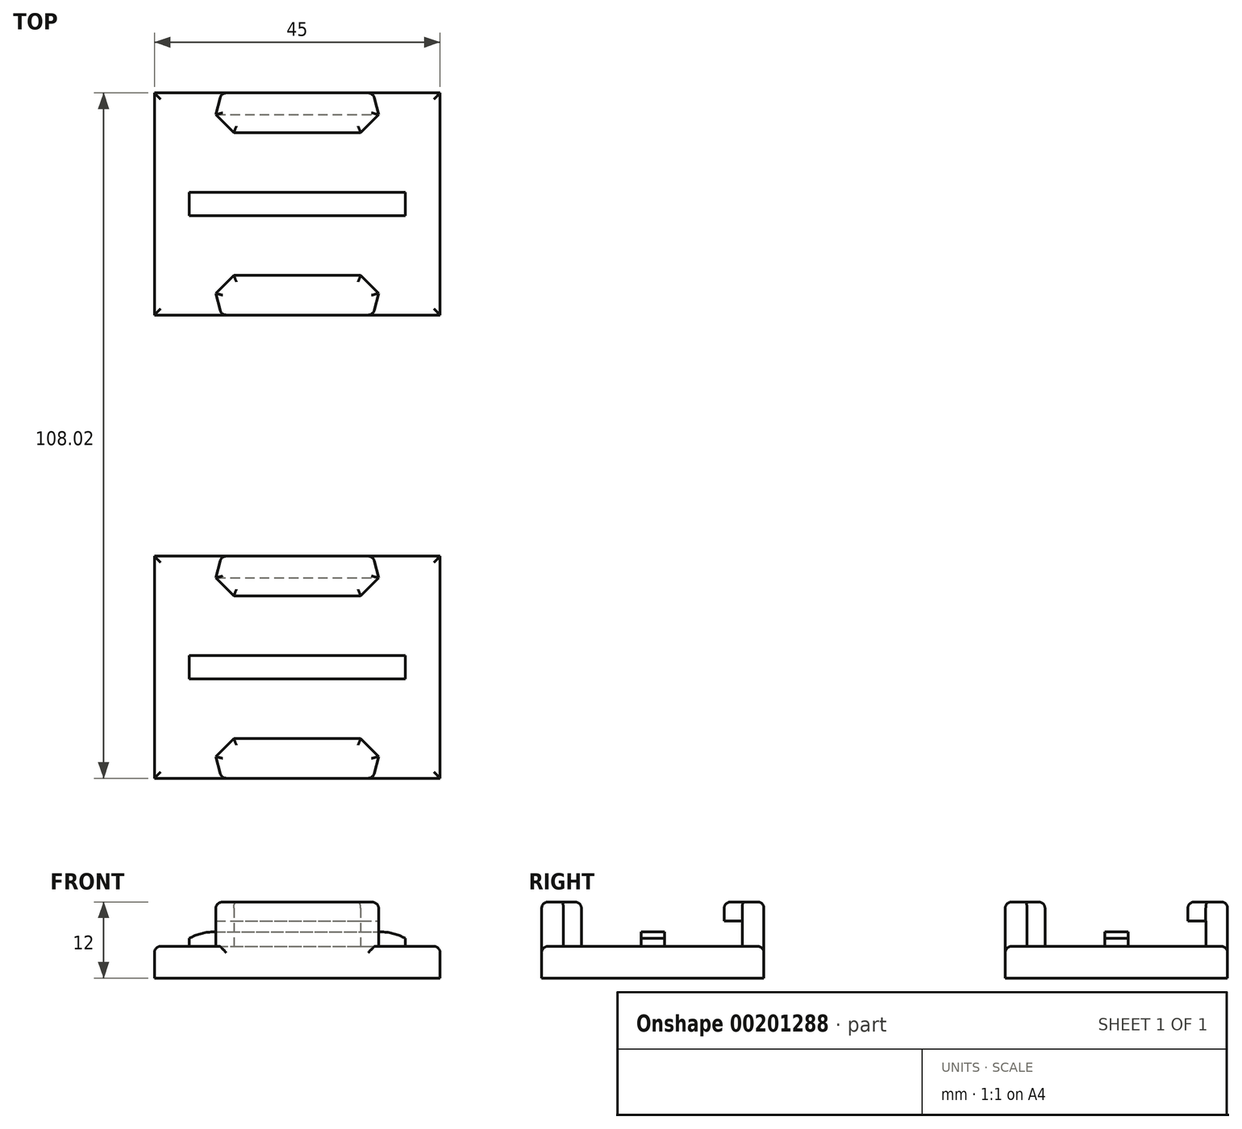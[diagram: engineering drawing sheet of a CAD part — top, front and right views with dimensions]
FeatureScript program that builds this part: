
annotation { "Feature Type Name" : "Feature", "Feature Type Description" : "" }
export const myFeature = defineFeature(function(context is Context, id is Id, definition is map)
    precondition{}
    {
        {
            var Q0;
            Q0=qCreatedBy(makeId("Top.planeOp"),FACE);
            var sketch = newSketch(context, id + "F0", { "sketchPlane" : qUnion([Q0])});
            skLineSegment(sketch, "E0.rect.bottom", {"start": v(-22.5, 17.5) * mm, "end": v(22.5, 17.5) * mm});
            skLineSegment(sketch, "E0.rect.top", {"start": v(-22.5, -17.5) * mm, "end": v(22.5, -17.5) * mm});
            skLineSegment(sketch, "E0.rect.left", {"start": v(-22.5, 17.5) * mm, "end": v(-22.5, -17.5) * mm});
            skLineSegment(sketch, "E0.rect.right", {"start": v(22.5, 17.5) * mm, "end": v(22.5, -17.5) * mm});
            skPoint(sketch, "E0.rect.middle", {"position": v(0, 0) * mm});
            skSolve(sketch);
        }
        {
            var Q0;
            Q0=makeQuery(id+"F0.imprint","IMPRINT",FACE,{"disambiguationData":[TD([[makeQuery(id+"F0.imprint","IMPRINT",EDGE,{"derivedFrom":sQuery(id+"F0.wireOp",EDGE,"E0.rect.bottom")}),-1.0]])]});
            extrude(context, id + "F1", {"entities" : qUnion([Q0]), "depth" : 5 * mm});
        }
        {
            var Q0;
            Q0=makeQuery(id+"F1.opExtrude","CAP_FACE",FACE,{"disambiguationData":[OSD([sQuery(id+"F0.wireOp",EDGE,"E0.rect.bottom"),sQuery(id+"F0.wireOp",EDGE,"E0.rect.top"),sQuery(id+"F0.wireOp",EDGE,"E0.rect.left"),sQuery(id+"F0.wireOp",EDGE,"E0.rect.right")])],"isStart":false});
            var sketch = newSketch(context, id + "F2", { "sketchPlane" : qUnion([Q0])});
            skLineSegment(sketch, "E1.rect.bottom", {"start": v(-17, 1.82) * mm, "end": v(17, 1.82) * mm});
            skLineSegment(sketch, "E1.rect.top", {"start": v(-17, -1.83) * mm, "end": v(17, -1.83) * mm});
            skLineSegment(sketch, "E1.rect.left", {"start": v(-17, 1.82) * mm, "end": v(-17, -1.83) * mm});
            skLineSegment(sketch, "E1.rect.right", {"start": v(17, 1.82) * mm, "end": v(17, -1.83) * mm});
            skPoint(sketch, "E1.rect.middle", {"position": v(0, 0) * mm});
            skSolve(sketch);
        }
        {
            var Q0;
            Q0=makeQuery(id+"F2.imprint","IMPRINT",FACE,{"disambiguationData":[TD([[makeQuery(id+"F2.imprint","IMPRINT",EDGE,{"derivedFrom":sQuery(id+"F2.wireOp",EDGE,"E1.rect.bottom")}),-1.0]])]});
            extrude(context, id + "F3", {"entities" : qUnion([Q0]), "operationType" : NewBodyOperationType.ADD, "depth" : 2.25 * mm});
        }
        {
            var Q0;
            Q0=makeQuery(id+"F3.opExtrude","SWEPT_FACE",FACE,{"disambiguationData":[OSD([sQuery(id+"F2.wireOp",EDGE,"E1.rect.top")])]});
            var sketch = newSketch(context, id + "F4", { "sketchPlane" : qUnion([Q0])});
            skLineSegment(sketch, "E2", {"start": v(-17, 7.25) * mm, "end": v(17, 7.25) * mm, "construction": true});
            skLineSegment(sketch, "E3.0", {"start": v(-17, 6.25) * mm, "end": v(17, 6.25) * mm});
            skArc(sketch, "E4", {"start": v(-13.26, 7.25) * mm, "mid": v(-15.2, 7) * mm, "end": v(-17, 6.25) * mm});
            skLineSegment(sketch, "E5", {"start": v(0, 0) * mm, "end": v(0, 15.47) * mm, "construction": true});
            skArc(sketch, "E6.0.MirrorCS", {"start": v(13.26, 7.25) * mm, "mid": v(15.2, 7) * mm, "end": v(17, 6.25) * mm});
            skLineSegment(sketch, "E7", {"start": v(-17, 6.25) * mm, "end": v(-18.16, 6.25) * mm});
            skLineSegment(sketch, "E8", {"start": v(-18.16, 6.25) * mm, "end": v(-18.16, 8.7) * mm});
            skLineSegment(sketch, "E9", {"start": v(-18.16, 8.7) * mm, "end": v(-13.25, 8.7) * mm});
            skLineSegment(sketch, "E10", {"start": v(-13.25, 8.7) * mm, "end": v(-13.26, 7.25) * mm});
            skLineSegment(sketch, "E11", {"start": v(13.26, 7.25) * mm, "end": v(13.26, 8.4) * mm});
            skLineSegment(sketch, "E12", {"start": v(13.26, 8.4) * mm, "end": v(18.11, 8.4) * mm});
            skLineSegment(sketch, "E13", {"start": v(18.11, 8.4) * mm, "end": v(18.11, 6.28) * mm});
            skLineSegment(sketch, "E14", {"start": v(18.11, 6.28) * mm, "end": v(17, 6.25) * mm});
            skSolve(sketch);
        }
        {
            var Q0;
            {var subQ0=sQuery(id+"F2.wireOp",EDGE,"E1.rect.top");var subQ1=makeQuery(id+"F3.opExtrude","CAP_EDGE",EDGE,{"disambiguationData":[OSD([subQ0])],"isStart":false});var subQ2=sQuery(id+"F4.wireOp",EDGE,"E4");var subQ3=makeQuery(id+"F4.imprint","INTERSECT",VERTEX,{"derivedFrom":[subQ1,subQ2]});var subQ6=makeQuery(id+"F4.imprint","IMPRINT",EDGE,{"disambiguationData":[TD([[subQ3,1.0]])],"derivedFrom":subQ1});var subQ8=sQuery(id+"F4.wireOp",EDGE,"E7");var subQ13=sQuery(id+"F4.wireOp",EDGE,"E6.0.MirrorCS");var subQ18=makeQuery(id+"F4.imprint","INTERSECT",VERTEX,{"derivedFrom":[subQ1,subQ13]});var subQ19=makeQuery(id+"F4.imprint","IMPRINT",EDGE,{"disambiguationData":[TD([[subQ18,-1.0]])],"derivedFrom":subQ1});var subQ20=sQuery(id+"F4.wireOp",EDGE,"E11");Q0=qUnion([makeQuery(id+"F4.imprint","IMPRINT",FACE,{"disambiguationData":[TD([[makeQuery(id+"F4.imprint","IMPRINT",EDGE,{"derivedFrom":subQ8}),-1.0]])]}),makeQuery(id+"F4.imprint","IMPRINT",FACE,{"disambiguationData":[TD([[subQ6,-1.0]])]}),makeQuery(id+"F4.imprint","IMPRINT",FACE,{"disambiguationData":[TD([[makeQuery(id+"F4.imprint","IMPRINT",EDGE,{"derivedFrom":subQ20}),-1.0]])]}),makeQuery(id+"F4.imprint","IMPRINT",FACE,{"disambiguationData":[TD([[subQ19,-1.0]])]})]);}
            extrude(context, id + "F5", {"entities" : qUnion([Q0]), "operationType" : NewBodyOperationType.REMOVE, "endBound" : BoundingType.THROUGH_ALL, "oppositeDirection" : true, "depth" : 25 * mm});
        }
        {
            var Q0;
            Q0=makeQuery(id+"F1.opExtrude","CAP_FACE",FACE,{"disambiguationData":[OSD([sQuery(id+"F0.wireOp",EDGE,"E0.rect.bottom"),sQuery(id+"F0.wireOp",EDGE,"E0.rect.top"),sQuery(id+"F0.wireOp",EDGE,"E0.rect.left"),sQuery(id+"F0.wireOp",EDGE,"E0.rect.right")])],"isStart":false});
            var sketch = newSketch(context, id + "F6", { "sketchPlane" : qUnion([Q0])});
            skLineSegment(sketch, "E15.rect.bottom", {"start": v(-11.94, 17.5) * mm, "end": v(11.94, 17.5) * mm, "construction": true});
            skPoint(sketch, "E15.rect.middle", {"position": v(0, 0) * mm});
            skLineSegment(sketch, "E16.0", {"start": v(-10, 11.25) * mm, "end": v(10, 11.25) * mm});
            skLineSegment(sketch, "E17", {"start": v(-10, 11.25) * mm, "end": v(-12.82, 14.08) * mm, "construction": true});
            skLineSegment(sketch, "E18.0.MirrorCS", {"start": v(10, 11.25) * mm, "end": v(12.82, 14.08) * mm, "construction": true});
            skLineSegment(sketch, "E19", {"start": v(10, 11.25) * mm, "end": v(12.82, 14.08) * mm});
            skLineSegment(sketch, "E20", {"start": v(11.94, 17.5) * mm, "end": v(-11.94, 17.5) * mm});
            skLineSegment(sketch, "E21", {"start": v(-12.82, 14.08) * mm, "end": v(-10, 11.25) * mm});
            skLineSegment(sketch, "E22.0.MirrorCS", {"start": v(-10, -11.25) * mm, "end": v(-12.82, -14.08) * mm, "construction": true});
            skLineSegment(sketch, "E22.1.MirrorCS", {"start": v(-11.94, -17.5) * mm, "end": v(11.94, -17.5) * mm, "construction": true});
            skLineSegment(sketch, "E22.2.MirrorCS", {"start": v(-11.94, -17.5) * mm, "end": v(11.94, -17.5) * mm, "construction": true});
            skLineSegment(sketch, "E22.4.MirrorCS", {"start": v(-10, -11.25) * mm, "end": v(-12.82, -14.08) * mm, "construction": true});
            skLineSegment(sketch, "E22.5.MirrorCS", {"start": v(10, -11.25) * mm, "end": v(12.82, -14.08) * mm, "construction": true});
            skLineSegment(sketch, "E22.7.MirrorCS", {"start": v(11.94, -17.5) * mm, "end": v(-11.94, -17.5) * mm});
            skLineSegment(sketch, "E22.9.MirrorCS", {"start": v(10, -11.25) * mm, "end": v(12.82, -14.08) * mm});
            skLineSegment(sketch, "E22.10.MirrorCS", {"start": v(-12.82, -14.08) * mm, "end": v(-10, -11.25) * mm});
            skLineSegment(sketch, "E22.12.MirrorCS", {"start": v(-10, -11.25) * mm, "end": v(10, -11.25) * mm});
            skLineSegment(sketch, "E23", {"start": v(12.82, 14.08) * mm, "end": v(11.94, 17.5) * mm});
            skLineSegment(sketch, "E24.0.MirrorCS", {"start": v(12.82, -14.08) * mm, "end": v(11.94, -17.5) * mm});
            skLineSegment(sketch, "E25.0.MirrorCS", {"start": v(-12.82, 14.08) * mm, "end": v(-11.94, 17.5) * mm});
            skLineSegment(sketch, "E26.0.MirrorCS", {"start": v(-12.82, -14.08) * mm, "end": v(-11.94, -17.5) * mm});
            skSolve(sketch);
        }
        {
            var Q0;
            {Q0=qUnion([makeQuery(id+"F6.imprint","IMPRINT",FACE,{"disambiguationData":[TD([[makeQuery(id+"F6.imprint","IMPRINT",EDGE,{"derivedFrom":sQuery(id+"F6.wireOp",EDGE,"E16.0")}),1.0]])]}),makeQuery(id+"F6.imprint","IMPRINT",FACE,{"disambiguationData":[TD([[makeQuery(id+"F6.imprint","IMPRINT",EDGE,{"derivedFrom":sQuery(id+"F6.wireOp",EDGE,"E22.7.MirrorCS")}),1.0]])]})]);}
            extrude(context, id + "F7", {"entities" : qUnion([Q0]), "operationType" : NewBodyOperationType.ADD, "depth" : 7 * mm});
        }
        {
            var Q0;
            Q0=qCreatedBy(makeId("Right.planeOp"),FACE);
            var sketch = newSketch(context, id + "F8", { "sketchPlane" : qUnion([Q0])});
            skLineSegment(sketch, "E27.0", {"start": v(14.1, 9) * mm, "end": v(14.1, 5) * mm});
            skLineSegment(sketch, "E28.bottom", {"start": v(14.1, 5) * mm, "end": v(10.15, 5) * mm});
            skLineSegment(sketch, "E28.top", {"start": v(14.1, 9) * mm, "end": v(10.15, 9) * mm});
            skLineSegment(sketch, "E28.left", {"start": v(14.1, 5) * mm, "end": v(14.1, 9) * mm});
            skLineSegment(sketch, "E28.right", {"start": v(10.15, 5) * mm, "end": v(10.15, 9) * mm});
            skLineSegment(sketch, "E29.0.MirrorCS", {"start": v(-14.1, 5) * mm, "end": v(-14.1, 9) * mm});
            skLineSegment(sketch, "E29.1.MirrorCS", {"start": v(-14.1, 9) * mm, "end": v(-14.1, 5) * mm});
            skLineSegment(sketch, "E29.2.MirrorCS", {"start": v(-14.1, 9) * mm, "end": v(-10.15, 9) * mm});
            skLineSegment(sketch, "E29.3.MirrorCS", {"start": v(-10.15, 5) * mm, "end": v(-10.15, 9) * mm});
            skLineSegment(sketch, "E29.4.MirrorCS", {"start": v(-14.1, 5) * mm, "end": v(-10.15, 5) * mm});
            skSolve(sketch);
        }
        {
            var Q0;
            {Q0=qUnion([makeQuery(id+"F8.imprint","IMPRINT",FACE,{"disambiguationData":[TD([[makeQuery(id+"F8.imprint","IMPRINT",EDGE,{"derivedFrom":sQuery(id+"F8.wireOp",EDGE,"E28.bottom")}),-1.0]])]}),makeQuery(id+"F8.imprint","IMPRINT",FACE,{"disambiguationData":[TD([[makeQuery(id+"F8.imprint","IMPRINT",EDGE,{"derivedFrom":sQuery(id+"F8.wireOp",EDGE,"E29.1.MirrorCS")}),1.0]])]})]);}
            extrude(context, id + "F9", {"entities" : qUnion([Q0]), "operationType" : NewBodyOperationType.REMOVE, "endBound" : BoundingType.SYMMETRIC, "oppositeDirection" : true, "depth" : 31.01 * mm});
        }
        {
            var Q0;
            Q0=makeQuery(id+"F7.opExtrude","CAP_FACE",FACE,{"disambiguationData":[OSD([sQuery(id+"F6.wireOp",EDGE,"E16.0"),sQuery(id+"F6.wireOp",EDGE,"E19"),sQuery(id+"F6.wireOp",EDGE,"E20"),sQuery(id+"F6.wireOp",EDGE,"E21"),sQuery(id+"F6.wireOp",EDGE,"E23"),sQuery(id+"F6.wireOp",EDGE,"E25.0.MirrorCS")])],"isStart":false});
            var Q1;
            Q1=makeQuery(id+"F7.opExtrude","CAP_FACE",FACE,{"disambiguationData":[OSD([sQuery(id+"F6.wireOp",EDGE,"E22.7.MirrorCS"),sQuery(id+"F6.wireOp",EDGE,"E22.9.MirrorCS"),sQuery(id+"F6.wireOp",EDGE,"E22.10.MirrorCS"),sQuery(id+"F6.wireOp",EDGE,"E22.12.MirrorCS"),sQuery(id+"F6.wireOp",EDGE,"E24.0.MirrorCS"),sQuery(id+"F6.wireOp",EDGE,"E26.0.MirrorCS")])],"isStart":false});
            var Q2;
            Q2=makeQuery(id+"F7.opExtrude","SWEPT_EDGE",EDGE,{"disambiguationData":[OSD([sQuery(id+"F0.wireOp",EDGE,"E0.rect.bottom"),sQuery(id+"F6.wireOp",EDGE,"E20"),sQuery(id+"F6.wireOp",EDGE,"E23")])]});
            var Q3;
            Q3=makeQuery(id+"F7.opExtrude","SWEPT_EDGE",EDGE,{"disambiguationData":[OSD([sQuery(id+"F0.wireOp",EDGE,"E0.rect.bottom"),sQuery(id+"F6.wireOp",EDGE,"E20"),sQuery(id+"F6.wireOp",EDGE,"E25.0.MirrorCS")])]});
            var Q4;
            Q4=makeQuery(id+"F7.opExtrude","SWEPT_EDGE",EDGE,{"disambiguationData":[OSD([sQuery(id+"F0.wireOp",EDGE,"E0.rect.top"),sQuery(id+"F6.wireOp",EDGE,"E22.7.MirrorCS"),sQuery(id+"F6.wireOp",EDGE,"E24.0.MirrorCS")])]});
            var Q5;
            Q5=makeQuery(id+"F7.opExtrude","SWEPT_EDGE",EDGE,{"disambiguationData":[OSD([sQuery(id+"F0.wireOp",EDGE,"E0.rect.top"),sQuery(id+"F6.wireOp",EDGE,"E22.7.MirrorCS"),sQuery(id+"F6.wireOp",EDGE,"E26.0.MirrorCS")])]});
            fillet(context, id + "F10", {"entities" : qUnion([Q0, Q1, Q2, Q3, Q4, Q5]), "radius" : 1 * mm, "tangentPropagation" : true, "allowEdgeOverflow" : false});
        }
        {
            var Q0;
            {var subQ0=sQuery(id+"F0.wireOp",EDGE,"E0.rect.top");var subQ1=sQuery(id+"F0.wireOp",EDGE,"E0.rect.right");Q0=makeQuery(id+"F7.boolean.opBoolean","SPLIT",EDGE,{"disambiguationData":[TD([makeQuery(id+"F1.opExtrude","SWEPT_FACE",FACE,{"disambiguationData":[OSD([subQ1])]})])],"derivedFrom":makeQuery(id+"F1.opExtrude","CAP_EDGE",EDGE,{"disambiguationData":[OSD([subQ0])],"isStart":false})});}
            var Q1;
            Q1=makeQuery(id+"F1.opExtrude","CAP_EDGE",EDGE,{"disambiguationData":[OSD([sQuery(id+"F0.wireOp",EDGE,"E0.rect.right")])],"isStart":false});
            var Q2;
            {var subQ0=sQuery(id+"F0.wireOp",EDGE,"E0.rect.bottom");var subQ1=sQuery(id+"F0.wireOp",EDGE,"E0.rect.right");Q2=makeQuery(id+"F7.boolean.opBoolean","SPLIT",EDGE,{"disambiguationData":[TD([makeQuery(id+"F1.opExtrude","SWEPT_FACE",FACE,{"disambiguationData":[OSD([subQ1])]})])],"derivedFrom":makeQuery(id+"F1.opExtrude","CAP_EDGE",EDGE,{"disambiguationData":[OSD([subQ0])],"isStart":false})});}
            var Q3;
            {var subQ0=sQuery(id+"F0.wireOp",EDGE,"E0.rect.bottom");var subQ1=sQuery(id+"F0.wireOp",EDGE,"E0.rect.left");Q3=makeQuery(id+"F7.boolean.opBoolean","SPLIT",EDGE,{"disambiguationData":[TD([makeQuery(id+"F1.opExtrude","SWEPT_FACE",FACE,{"disambiguationData":[OSD([subQ1])]})])],"derivedFrom":makeQuery(id+"F1.opExtrude","CAP_EDGE",EDGE,{"disambiguationData":[OSD([subQ0])],"isStart":false})});}
            var Q4;
            Q4=makeQuery(id+"F1.opExtrude","CAP_EDGE",EDGE,{"disambiguationData":[OSD([sQuery(id+"F0.wireOp",EDGE,"E0.rect.left")])],"isStart":false});
            var Q5;
            {var subQ0=sQuery(id+"F0.wireOp",EDGE,"E0.rect.top");var subQ1=sQuery(id+"F0.wireOp",EDGE,"E0.rect.left");Q5=makeQuery(id+"F7.boolean.opBoolean","SPLIT",EDGE,{"disambiguationData":[TD([makeQuery(id+"F1.opExtrude","SWEPT_FACE",FACE,{"disambiguationData":[OSD([subQ1])]})])],"derivedFrom":makeQuery(id+"F1.opExtrude","CAP_EDGE",EDGE,{"disambiguationData":[OSD([subQ0])],"isStart":false})});}
            fillet(context, id + "F11", {"entities" : qUnion([Q0, Q1, Q2, Q3, Q4, Q5]), "radius" : 1 * mm, "allowEdgeOverflow" : false});
        }
        {
            var Q0;
            Q0=makeQuery(id+"F1.opExtrude","SWEPT_BODY",BODY,{"disambiguationData":[OSD([sQuery(id+"F0.wireOp",EDGE,"E0.rect.bottom"),sQuery(id+"F0.wireOp",EDGE,"E0.rect.top"),sQuery(id+"F0.wireOp",EDGE,"E0.rect.left"),sQuery(id+"F0.wireOp",EDGE,"E0.rect.right")])]});
            transform(context, id + "F12", {"entities" : qUnion([Q0]), "transformType" : TransformType.TRANSLATION_3D, "dx" : 0 * mm, "dy" : 73.02 * mm, "dz" : 0 * mm, "makeCopy" : true});
        }
    });
